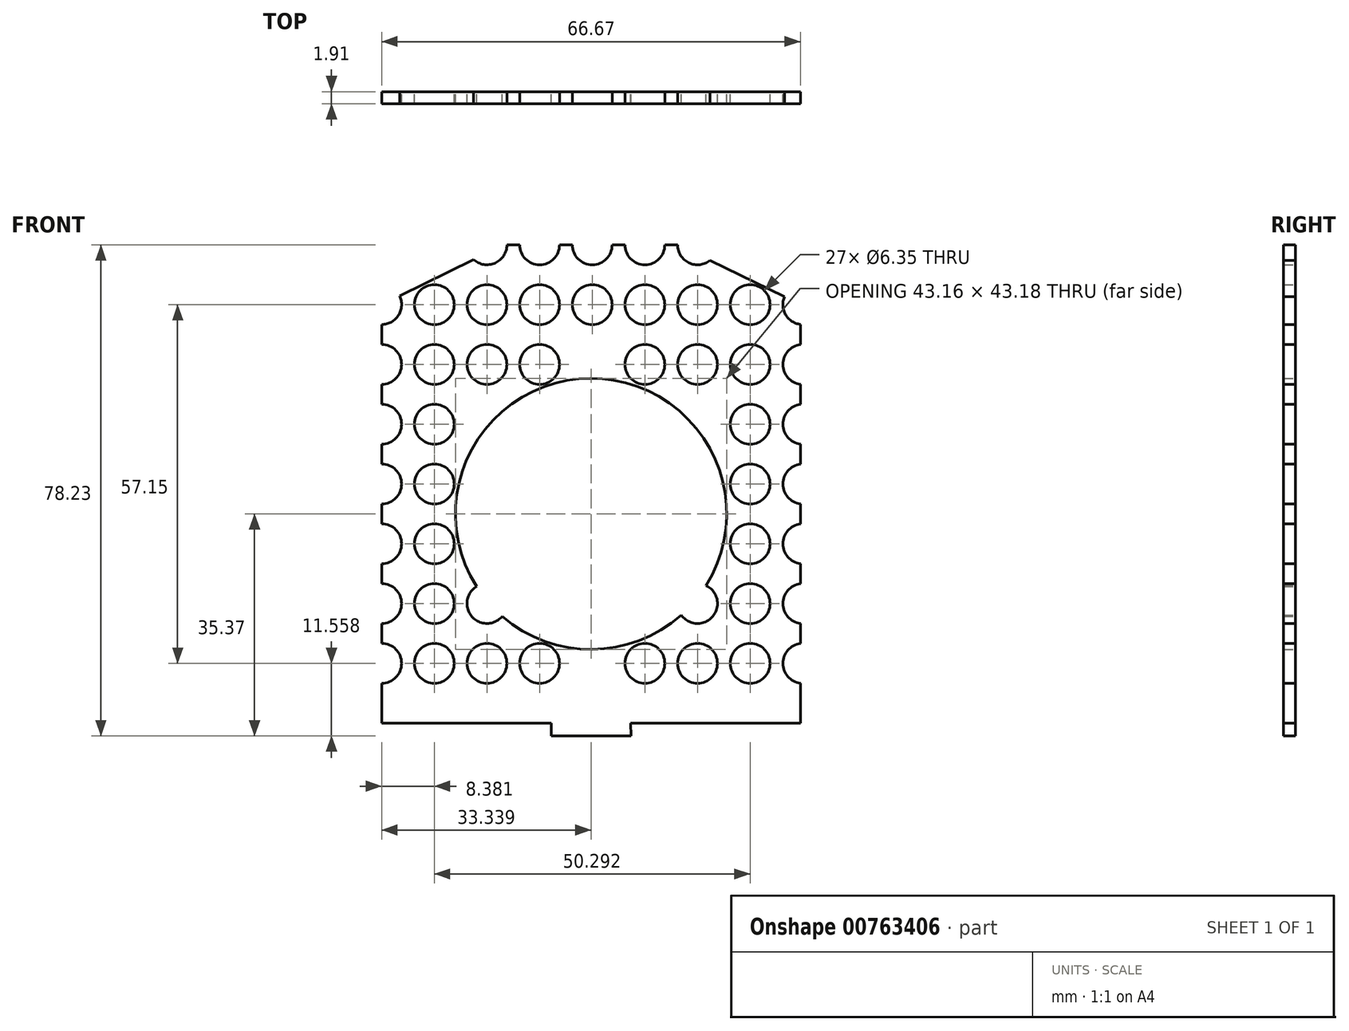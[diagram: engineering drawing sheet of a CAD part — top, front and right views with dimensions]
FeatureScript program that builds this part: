
annotation { "Feature Type Name" : "Feature", "Feature Type Description" : "" }
export const myFeature = defineFeature(function(context is Context, id is Id, definition is map)
    precondition{}
    {
        {
            var Q0;
            Q0=qCreatedBy(makeId("Front.planeOp"),FACE);
            var sketch = newSketch(context, id + "F0", { "sketchPlane" : qUnion([Q0])});
            skLineSegment(sketch, "E0", {"start": v(-62.95, -34.15) * mm, "end": v(-62.95, -27.8) * mm});
            skArc(sketch, "E1", {"start": v(-11.3, -12.23) * mm, "mid": v(-29.7, 20.78) * mm, "end": v(-47.84, -12.39) * mm});
            skLineSegment(sketch, "E2", {"start": v(-60.1, 33.93) * mm, "end": v(-48.32, 39.7) * mm});
            skLineSegment(sketch, "E3", {"start": v(-10.67, 39.58) * mm, "end": v(1.18, 33.77) * mm});
            skArc(sketch, "E4.0.1.0", {"start": v(-62.95, -27.8) * mm, "mid": v(-59.78, -24.62) * mm, "end": v(-62.95, -21.45) * mm});
            skArc(sketch, "E4.0.2.0", {"start": v(-62.95, -18.27) * mm, "mid": v(-59.78, -15.1) * mm, "end": v(-62.95, -11.92) * mm});
            skArc(sketch, "E4.0.3.0", {"start": v(-62.95, -8.75) * mm, "mid": v(-59.78, -5.57) * mm, "end": v(-62.95, -2.4) * mm});
            skArc(sketch, "E4.0.4.0", {"start": v(-62.95, 0.78) * mm, "mid": v(-59.78, 3.95) * mm, "end": v(-62.95, 7.13) * mm});
            skArc(sketch, "E4.0.5.0", {"start": v(-62.95, 10.3) * mm, "mid": v(-59.78, 13.48) * mm, "end": v(-62.95, 16.65) * mm});
            skArc(sketch, "E4.0.6.0", {"start": v(-62.95, 19.83) * mm, "mid": v(-59.78, 23) * mm, "end": v(-62.95, 26.18) * mm});
            skArc(sketch, "E4.0.7.0", {"start": v(-62.95, 29.35) * mm, "mid": v(-60.26, 30.85) * mm, "end": v(-60.1, 33.93) * mm});
            skCircle(sketch, "E4.1.1.0", {"center": v(-54.57, -24.62) * mm, "radius": 3.18 * mm});
            skCircle(sketch, "E4.1.2.0", {"center": v(-54.57, -15.1) * mm, "radius": 3.18 * mm});
            skCircle(sketch, "E4.1.3.0", {"center": v(-54.57, -5.57) * mm, "radius": 3.18 * mm});
            skCircle(sketch, "E4.1.4.0", {"center": v(-54.57, 3.95) * mm, "radius": 3.18 * mm});
            skCircle(sketch, "E4.1.5.0", {"center": v(-54.57, 13.48) * mm, "radius": 3.18 * mm});
            skCircle(sketch, "E4.1.6.0", {"center": v(-54.57, 23) * mm, "radius": 3.18 * mm});
            skCircle(sketch, "E4.1.7.0", {"center": v(-54.57, 32.53) * mm, "radius": 3.18 * mm});
            skCircle(sketch, "E4.2.1.0", {"center": v(-46.19, -24.62) * mm, "radius": 3.18 * mm});
            skArc(sketch, "E4.2.2.0", {"start": v(-47.84, -12.39) * mm, "mid": v(-48.6, -17.17) * mm, "end": v(-43.75, -17.13) * mm});
            skCircle(sketch, "E4.2.6.0", {"center": v(-46.19, 23) * mm, "radius": 3.18 * mm});
            skCircle(sketch, "E4.2.7.0", {"center": v(-46.19, 32.53) * mm, "radius": 3.18 * mm});
            skArc(sketch, "E4.2.8.0", {"start": v(-48.32, 39.7) * mm, "mid": v(-44.9, 39.15) * mm, "end": v(-43.01, 42.05) * mm});
            skCircle(sketch, "E4.3.1.0", {"center": v(-37.8, -24.62) * mm, "radius": 3.18 * mm});
            skCircle(sketch, "E4.3.6.0", {"center": v(-37.8, 23) * mm, "radius": 3.18 * mm});
            skCircle(sketch, "E4.3.7.0", {"center": v(-37.8, 32.53) * mm, "radius": 3.18 * mm});
            skArc(sketch, "E4.3.8.0", {"start": v(-40.98, 42.05) * mm, "mid": v(-37.8, 38.88) * mm, "end": v(-34.63, 42.05) * mm});
            skCircle(sketch, "E4.4.7.0", {"center": v(-29.42, 32.53) * mm, "radius": 3.18 * mm});
            skArc(sketch, "E4.4.8.0", {"start": v(-32.6, 42.05) * mm, "mid": v(-29.42, 38.88) * mm, "end": v(-26.25, 42.05) * mm});
            skCircle(sketch, "E4.5.1.0", {"center": v(-21.04, -24.62) * mm, "radius": 3.18 * mm});
            skCircle(sketch, "E4.5.6.0", {"center": v(-21.04, 23) * mm, "radius": 3.18 * mm});
            skCircle(sketch, "E4.5.7.0", {"center": v(-21.04, 32.53) * mm, "radius": 3.18 * mm});
            skArc(sketch, "E4.5.8.0", {"start": v(-24.22, 42.05) * mm, "mid": v(-21.04, 38.88) * mm, "end": v(-17.87, 42.05) * mm});
            skCircle(sketch, "E4.6.1.0", {"center": v(-12.66, -24.62) * mm, "radius": 3.18 * mm});
            skArc(sketch, "E4.6.2.0", {"start": v(-15.25, -16.93) * mm, "mid": v(-10.23, -17.14) * mm, "end": v(-11.3, -12.23) * mm});
            skCircle(sketch, "E4.6.6.0", {"center": v(-12.66, 23) * mm, "radius": 3.18 * mm});
            skCircle(sketch, "E4.6.7.0", {"center": v(-12.66, 32.53) * mm, "radius": 3.18 * mm});
            skArc(sketch, "E4.6.8.0", {"start": v(-15.83, 42.05) * mm, "mid": v(-14.03, 39.19) * mm, "end": v(-10.67, 39.58) * mm});
            skCircle(sketch, "E4.7.1.0", {"center": v(-4.28, -24.62) * mm, "radius": 3.18 * mm});
            skCircle(sketch, "E4.7.2.0", {"center": v(-4.28, -15.1) * mm, "radius": 3.18 * mm});
            skCircle(sketch, "E4.7.3.0", {"center": v(-4.28, -5.57) * mm, "radius": 3.18 * mm});
            skCircle(sketch, "E4.7.4.0", {"center": v(-4.28, 3.95) * mm, "radius": 3.18 * mm});
            skCircle(sketch, "E4.7.5.0", {"center": v(-4.28, 13.48) * mm, "radius": 3.18 * mm});
            skCircle(sketch, "E4.7.6.0", {"center": v(-4.28, 23) * mm, "radius": 3.18 * mm});
            skCircle(sketch, "E4.7.7.0", {"center": v(-4.28, 32.53) * mm, "radius": 3.18 * mm});
            skArc(sketch, "E4.8.1.0", {"start": v(3.72, -21.47) * mm, "mid": v(0.93, -24.62) * mm, "end": v(3.72, -27.77) * mm});
            skArc(sketch, "E4.8.2.0", {"start": v(3.72, -11.95) * mm, "mid": v(0.93, -15.1) * mm, "end": v(3.72, -18.25) * mm});
            skArc(sketch, "E4.8.3.0", {"start": v(3.72, -2.42) * mm, "mid": v(0.93, -5.57) * mm, "end": v(3.72, -8.72) * mm});
            skArc(sketch, "E4.8.4.0", {"start": v(3.72, 7.1) * mm, "mid": v(0.93, 3.95) * mm, "end": v(3.72, 0.8) * mm});
            skArc(sketch, "E4.8.5.0", {"start": v(3.72, 16.63) * mm, "mid": v(0.93, 13.48) * mm, "end": v(3.72, 10.33) * mm});
            skArc(sketch, "E4.8.6.0", {"start": v(3.72, 26.15) * mm, "mid": v(0.93, 23) * mm, "end": v(3.72, 19.85) * mm});
            skArc(sketch, "E4.8.7.0", {"start": v(1.18, 33.77) * mm, "mid": v(1.36, 30.94) * mm, "end": v(3.72, 29.38) * mm});
            skLineSegment(sketch, "E4.direction1", {"start": v(-62.95, -34.15) * mm, "end": v(-54.57, -34.15) * mm, "construction": true});
            skLineSegment(sketch, "E4.direction2", {"start": v(-62.95, -34.15) * mm, "end": v(-62.95, -27.8) * mm, "construction": true});
            skLineSegment(sketch, "E5.trimOffspring", {"start": v(-62.95, 26.18) * mm, "end": v(-62.95, 29.35) * mm});
            skLineSegment(sketch, "E6.trimOffspring", {"start": v(-62.95, 16.65) * mm, "end": v(-62.95, 19.83) * mm});
            skLineSegment(sketch, "E7.trimOffspring", {"start": v(-62.95, 7.13) * mm, "end": v(-62.95, 10.3) * mm});
            skLineSegment(sketch, "E8.trimOffspring", {"start": v(-62.95, -2.4) * mm, "end": v(-62.95, 0.78) * mm});
            skLineSegment(sketch, "E9.trimOffspring", {"start": v(-62.95, -11.92) * mm, "end": v(-62.95, -8.75) * mm});
            skLineSegment(sketch, "E10.trimOffspring", {"start": v(-62.95, -21.45) * mm, "end": v(-62.95, -18.27) * mm});
            skLineSegment(sketch, "E11.trimOffspring", {"start": v(3.72, -2.42) * mm, "end": v(3.72, 0.8) * mm});
            skLineSegment(sketch, "E12.trimOffspring", {"start": v(3.72, 7.1) * mm, "end": v(3.72, 10.33) * mm});
            skLineSegment(sketch, "E13.trimOffspring", {"start": v(3.72, 16.63) * mm, "end": v(3.72, 19.85) * mm});
            skLineSegment(sketch, "E14.trimOffspring", {"start": v(3.72, 26.15) * mm, "end": v(3.72, 29.38) * mm});
            skLineSegment(sketch, "E15.trimOffspring", {"start": v(-17.87, 42.05) * mm, "end": v(-15.71, 42.05) * mm});
            skLineSegment(sketch, "E16.trimOffspring", {"start": v(-26.25, 42.05) * mm, "end": v(-24.22, 42.05) * mm});
            skLineSegment(sketch, "E17.trimOffspring", {"start": v(-34.63, 42.05) * mm, "end": v(-32.6, 42.05) * mm});
            skLineSegment(sketch, "E18", {"start": v(3.72, -34.15) * mm, "end": v(3.72, -27.77) * mm});
            skLineSegment(sketch, "E19", {"start": v(3.72, -21.47) * mm, "end": v(3.72, -18.25) * mm});
            skLineSegment(sketch, "E20", {"start": v(3.72, -11.95) * mm, "end": v(3.72, -8.72) * mm});
            skArc(sketch, "E21.trimOffspring", {"start": v(-43.75, -17.13) * mm, "mid": v(-29.46, -22.4) * mm, "end": v(-15.25, -16.93) * mm});
            skLineSegment(sketch, "E22", {"start": v(-43.01, 42.05) * mm, "end": v(-40.98, 42.05) * mm});
            skLineSegment(sketch, "E23", {"start": v(-62.95, -34.15) * mm, "end": v(-62.95, -32.12) * mm});
            skLineSegment(sketch, "E24", {"start": v(-62.95, -34.15) * mm, "end": v(-35.96, -34.15) * mm});
            skLineSegment(sketch, "E25", {"start": v(-35.96, -36.18) * mm, "end": v(-23.26, -36.18) * mm});
            skLineSegment(sketch, "E26", {"start": v(-23.26, -36.18) * mm, "end": v(-23.3, -34.15) * mm});
            skLineSegment(sketch, "E27", {"start": v(3.72, -34.15) * mm, "end": v(-23.3, -34.15) * mm});
            skLineSegment(sketch, "E28", {"start": v(-35.96, -36.18) * mm, "end": v(-35.96, -34.15) * mm});
            skSolve(sketch);
        }
        {
            var Q0;
            Q0=makeQuery(id+"F0.imprint","IMPRINT",FACE,{"disambiguationData":[TD([[makeQuery(id+"F0.imprint","IMPRINT",EDGE,{"derivedFrom":sQuery(id+"F0.wireOp",EDGE,"E0")}),-1.0]])]});
            extrude(context, id + "F1", {"entities" : qUnion([Q0]), "depth" : 1.9 * mm, "offsetDistance" : 25.4 * mm});
        }
    });
